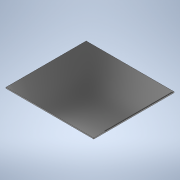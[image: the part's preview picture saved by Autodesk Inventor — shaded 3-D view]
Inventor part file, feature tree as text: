
AUTODESK INVENTOR PART (.ipt)
format: ipt  version: 2022 (Build 260153000, 153)  size: 804,864 bytes
history: native  units: in
note: dims shown in document units (in); Inventor stores cm internally (conversion verified against a paired STEP export)
features: sketch x3, extrude x2
ambient origin geometry x8: Origin, YZ Plane, XZ Plane, XY Plane, X Axis, Y Axis, Z Axis, Center Point
bodies: Solid1 (feature_tree)
feature tree (5):
  sketch  "Sketch1"  dims[d0=0.8268in d1=0.9055in]
  extrude  "Extrusion1"  Depth=0.9055in
  extrude  "Extrusion2"  Depth=0.0059in
  sketch  "Sketch2"  dims[d2=0.0098in d3=0.0in d4=0.0059in]
  sketch  "Sketch3"  dims[d5=0.0031in d6=55.9055in d8=0.0049in d9=0.3937in d11=0.3937in d13=0.1181in d14=0.002in d15=0.0264in d16=0.0004in d17=0.0in]
